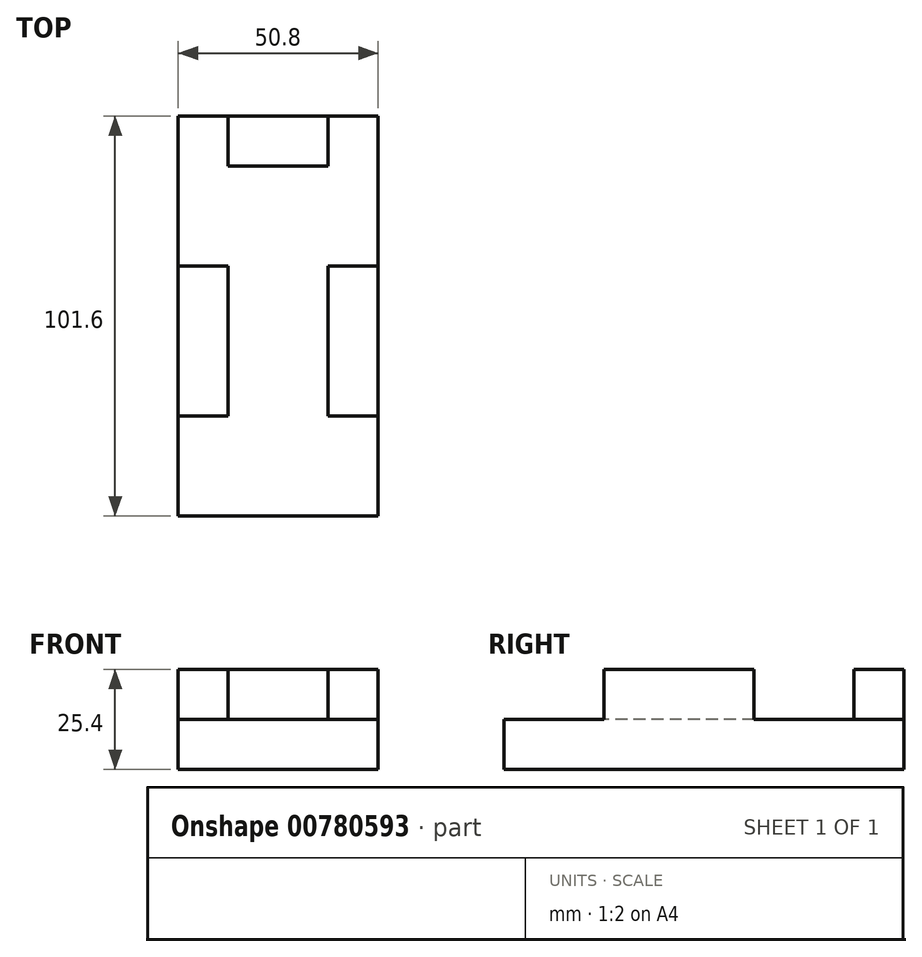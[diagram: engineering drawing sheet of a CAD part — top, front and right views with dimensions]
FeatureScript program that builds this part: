
annotation { "Feature Type Name" : "Feature", "Feature Type Description" : "" }
export const myFeature = defineFeature(function(context is Context, id is Id, definition is map)
    precondition{}
    {
        {
            var Q0;
            Q0=qCreatedBy(makeId("Top.planeOp"),FACE);
            var sketch = newSketch(context, id + "F0", { "sketchPlane" : qUnion([Q0])});
            skLineSegment(sketch, "E0.bottom", {"start": v(-41.43, 54.96) * mm, "end": v(9.37, 54.96) * mm});
            skLineSegment(sketch, "E0.top", {"start": v(-41.43, -46.64) * mm, "end": v(9.37, -46.64) * mm});
            skLineSegment(sketch, "E0.left", {"start": v(-41.43, 54.96) * mm, "end": v(-41.43, -46.64) * mm});
            skLineSegment(sketch, "E0.right", {"start": v(9.37, 54.96) * mm, "end": v(9.37, -46.64) * mm});
            skSolve(sketch);
        }
        {
            var Q0;
            Q0 = qSketchRegion(id + "F0", true);
            extrude(context, id + "F1", {"entities" : qUnion([Q0]), "depth" : 12.7 * mm, "offsetDistance" : 25.4 * mm});
        }
        {
            var Q0;
            Q0=makeQuery(id+"F1.opExtrude","CAP_FACE",FACE,{"disambiguationData":[OSD([sQuery(id+"F0.wireOp",EDGE,"E0.bottom"),sQuery(id+"F0.wireOp",EDGE,"E0.top"),sQuery(id+"F0.wireOp",EDGE,"E0.left"),sQuery(id+"F0.wireOp",EDGE,"E0.right")])],"isStart":false});
            var sketch = newSketch(context, id + "F2", { "sketchPlane" : qUnion([Q0])});
            skLineSegment(sketch, "E1.bottom", {"start": v(-28.73, 54.96) * mm, "end": v(-3.33, 54.96) * mm});
            skLineSegment(sketch, "E1.top", {"start": v(-28.73, 42.26) * mm, "end": v(-3.33, 42.26) * mm});
            skLineSegment(sketch, "E1.left", {"start": v(-28.73, 54.96) * mm, "end": v(-28.73, 42.26) * mm});
            skLineSegment(sketch, "E1.right", {"start": v(-3.33, 54.96) * mm, "end": v(-3.33, 42.26) * mm});
            skLineSegment(sketch, "E2.bottom", {"start": v(-41.43, -21.24) * mm, "end": v(-28.73, -21.24) * mm});
            skLineSegment(sketch, "E2.top", {"start": v(-41.43, 16.86) * mm, "end": v(-28.73, 16.86) * mm});
            skLineSegment(sketch, "E2.left", {"start": v(-41.43, -21.24) * mm, "end": v(-41.43, 16.86) * mm});
            skLineSegment(sketch, "E2.right", {"start": v(9.37, -21.24) * mm, "end": v(9.37, 16.86) * mm});
            skLineSegment(sketch, "E3.left", {"start": v(-28.73, 16.86) * mm, "end": v(-28.73, -21.24) * mm});
            skLineSegment(sketch, "E3.right", {"start": v(-3.33, 16.86) * mm, "end": v(-3.33, -21.24) * mm});
            skLineSegment(sketch, "E4.trimOffspring", {"start": v(-3.33, 16.86) * mm, "end": v(9.37, 16.86) * mm});
            skLineSegment(sketch, "E5.trimOffspring", {"start": v(-3.33, -21.24) * mm, "end": v(9.37, -21.24) * mm});
            skSolve(sketch);
        }
        {
            var Q0;
            Q0 = qSketchRegion(id + "F2", true);
            extrude(context, id + "F3", {"entities" : qUnion([Q0]), "operationType" : NewBodyOperationType.ADD, "depth" : 12.7 * mm, "offsetDistance" : 25.4 * mm});
        }
    });
